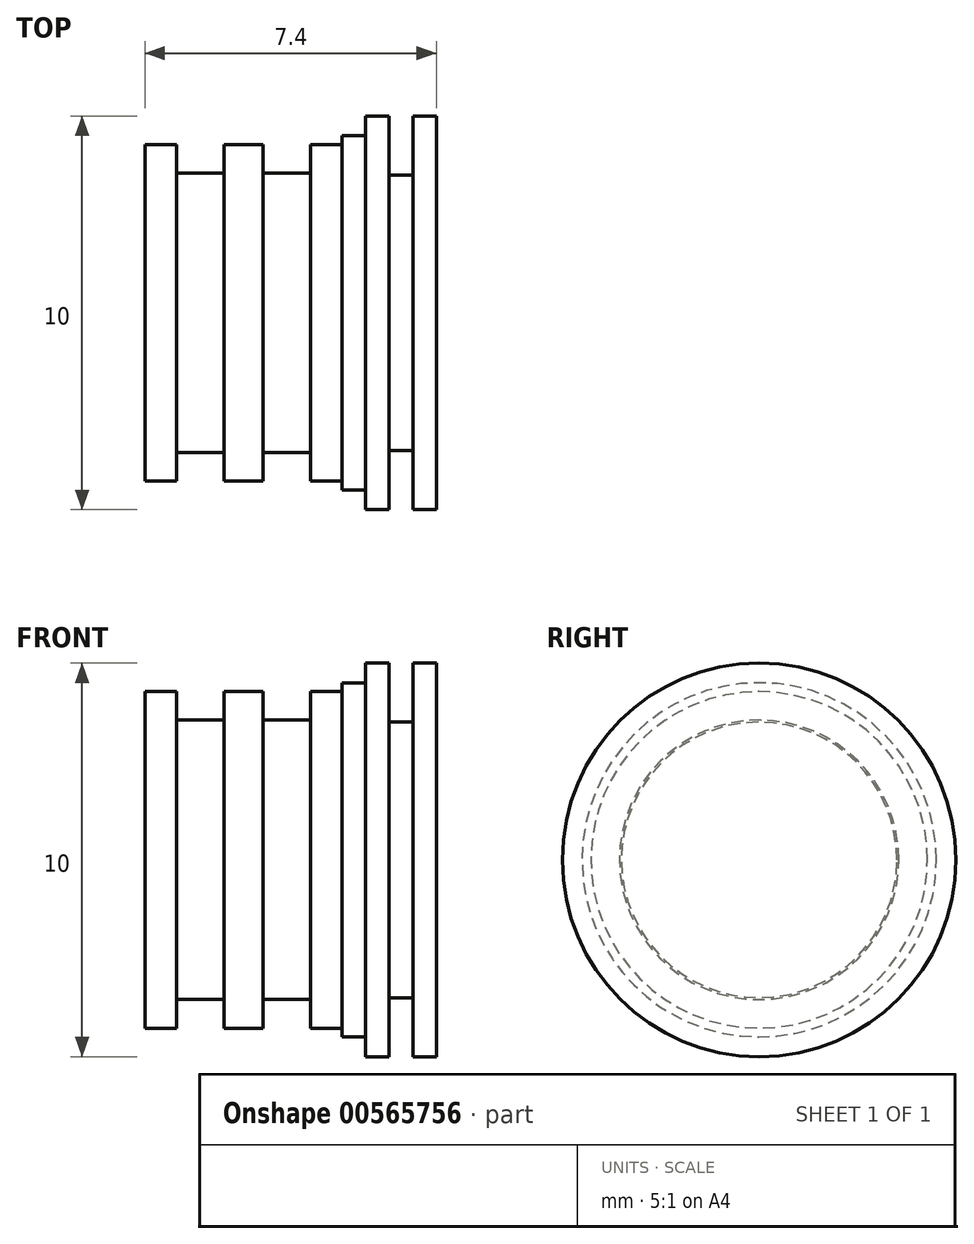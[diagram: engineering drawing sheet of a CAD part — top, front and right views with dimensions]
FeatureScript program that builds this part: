
annotation { "Feature Type Name" : "Feature", "Feature Type Description" : "" }
export const myFeature = defineFeature(function(context is Context, id is Id, definition is map)
    precondition{}
    {
        {
            var Q0;
            Q0=qCreatedBy(makeId("Front.planeOp"),FACE);
            var sketch = newSketch(context, id + "F0", { "sketchPlane" : qUnion([Q0])});
            skLineSegment(sketch, "E0", {"start": v(-6.2, 4.28) * mm, "end": v(-6.2, -4.28) * mm});
            skLineSegment(sketch, "E1", {"start": v(-6.2, -4.27) * mm, "end": v(-5.4, -4.27) * mm});
            skLineSegment(sketch, "E2", {"start": v(-5.4, -4.28) * mm, "end": v(-5.4, -3.55) * mm});
            skLineSegment(sketch, "E3", {"start": v(-5.4, -3.55) * mm, "end": v(-4.2, -3.55) * mm});
            skLineSegment(sketch, "E4", {"start": v(-4.2, -3.55) * mm, "end": v(-4.2, -4.28) * mm});
            skLineSegment(sketch, "E5", {"start": v(-4.2, -4.27) * mm, "end": v(-3.2, -4.27) * mm});
            skLineSegment(sketch, "E6", {"start": v(-3.2, -4.28) * mm, "end": v(-3.2, -3.55) * mm});
            skLineSegment(sketch, "E7", {"start": v(-3.2, -3.55) * mm, "end": v(-2, -3.55) * mm});
            skLineSegment(sketch, "E8", {"start": v(-2, -3.55) * mm, "end": v(-2, -4.28) * mm});
            skLineSegment(sketch, "E9", {"start": v(-2, -4.27) * mm, "end": v(-1.2, -4.27) * mm});
            skLineSegment(sketch, "E10", {"start": v(-1.2, -4.27) * mm, "end": v(-1.2, -4.5) * mm});
            skLineSegment(sketch, "E11", {"start": v(-1.2, -4.5) * mm, "end": v(-0.6, -4.5) * mm});
            skLineSegment(sketch, "E12", {"start": v(-0.6, -4.5) * mm, "end": v(-0.6, -5) * mm});
            skLineSegment(sketch, "E13", {"start": v(-0.6, -5) * mm, "end": v(0, -5) * mm});
            skLineSegment(sketch, "E14", {"start": v(0, -5) * mm, "end": v(0, -3.5) * mm});
            skLineSegment(sketch, "E15", {"start": v(0, -3.5) * mm, "end": v(0.6, -3.5) * mm});
            skLineSegment(sketch, "E16", {"start": v(0.6, -3.5) * mm, "end": v(0.6, -5) * mm});
            skLineSegment(sketch, "E17", {"start": v(0.6, -5) * mm, "end": v(1.2, -5) * mm});
            skLineSegment(sketch, "E18", {"start": v(1.2, -5) * mm, "end": v(1.2, 5) * mm});
            skLineSegment(sketch, "E19", {"start": v(1.2, 5) * mm, "end": v(0.6, 5) * mm});
            skLineSegment(sketch, "E20", {"start": v(0.6, 3.5) * mm, "end": v(0, 3.5) * mm});
            skLineSegment(sketch, "E21", {"start": v(0, 5) * mm, "end": v(-0.6, 5) * mm});
            skLineSegment(sketch, "E22", {"start": v(-0.6, 5) * mm, "end": v(-0.6, 4.5) * mm});
            skLineSegment(sketch, "E23", {"start": v(-0.6, 4.5) * mm, "end": v(-1.2, 4.5) * mm});
            skLineSegment(sketch, "E24", {"start": v(-1.2, 4.5) * mm, "end": v(-1.2, 4.27) * mm});
            skLineSegment(sketch, "E25", {"start": v(-1.2, 4.28) * mm, "end": v(-2, 4.28) * mm});
            skLineSegment(sketch, "E26", {"start": v(-2, 4.28) * mm, "end": v(-2, 3.55) * mm});
            skLineSegment(sketch, "E27", {"start": v(-2, 3.55) * mm, "end": v(-3.2, 3.55) * mm});
            skLineSegment(sketch, "E28", {"start": v(-3.2, 3.55) * mm, "end": v(-3.2, 4.28) * mm});
            skLineSegment(sketch, "E29", {"start": v(-3.2, 4.28) * mm, "end": v(-4.2, 4.28) * mm});
            skLineSegment(sketch, "E30", {"start": v(-4.2, 4.28) * mm, "end": v(-4.2, 3.55) * mm});
            skLineSegment(sketch, "E31", {"start": v(-4.2, 3.55) * mm, "end": v(-5.4, 3.55) * mm});
            skLineSegment(sketch, "E32", {"start": v(-5.4, 3.55) * mm, "end": v(-5.4, 4.28) * mm});
            skLineSegment(sketch, "E33", {"start": v(-5.4, 4.28) * mm, "end": v(-6.2, 4.28) * mm});
            skLineSegment(sketch, "E34", {"start": v(0.6, 5) * mm, "end": v(0.6, 3.5) * mm});
            skLineSegment(sketch, "E35", {"start": v(0, 3.5) * mm, "end": v(0, 5) * mm});
            skLineSegment(sketch, "E36", {"start": v(-17.8, 0) * mm, "end": v(9.4, 0) * mm});
            skSolve(sketch);
        }
        {
            var Q0;
            {var subQ4=sQuery(id+"F0.wireOp",EDGE,"E19");Q0=makeQuery(id+"F0.imprint","IMPRINT",FACE,{"disambiguationData":[TD([[makeQuery(id+"F0.imprint","IMPRINT",EDGE,{"derivedFrom":subQ4}),1.0]])]});}
            var Q1;
            Q1=sQuery(id+"F0.wireOp",EDGE,"E36");
            revolve(context, id + "F1", {"surfaceOperationType" : NewSurfaceOperationType.NEW, "entities" : qUnion([Q0]), "axis" : qUnion([Q1]), "revolveType" : RevolveType.FULL});
        }
    });
